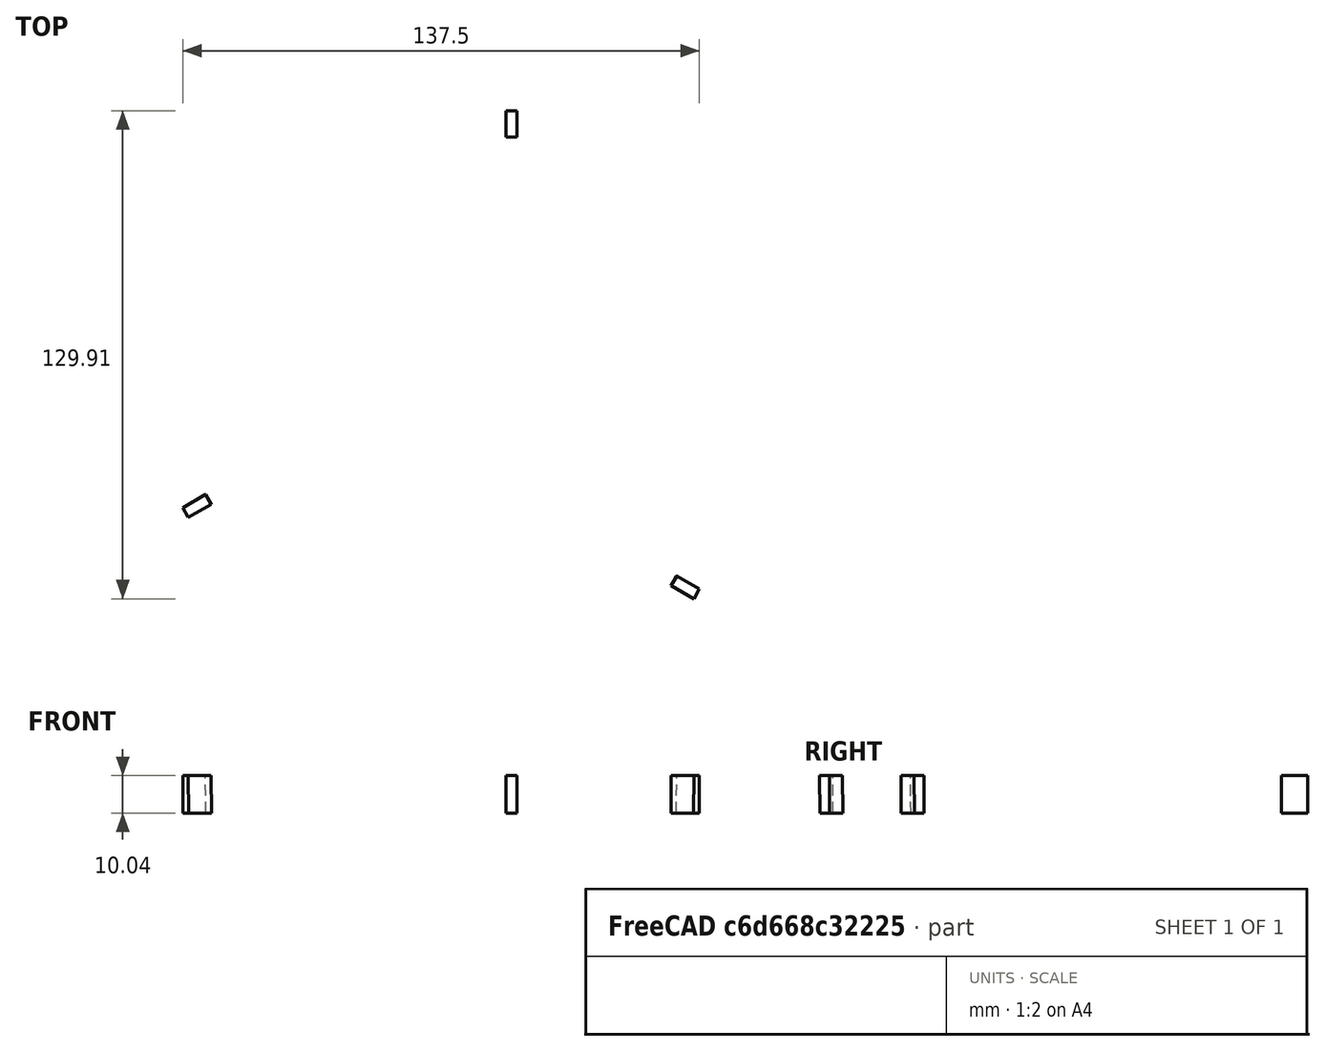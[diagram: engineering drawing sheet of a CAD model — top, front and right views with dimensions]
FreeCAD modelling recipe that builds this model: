
FCSTD DOCUMENT  (FreeCAD 2024.1R35694 (Git))
Label: spreadsheet-example-deltarobot
License: All rights reserved
LicenseURL: http://en.wikipedia.org/wiki/All_rights_reserved
objects: App::FeaturePython×23, App::Link×17, Part::FeaturePython×3, Spreadsheet::Sheet×1, Assembly::JointGroup×1, Assembly::AssemblyObject×1
note: 3 computed .brp shape members not serialized (recipe doc carries the construction recipe); baked Part::Feature solids carry a one-line shape summary decoded from their .brp
EXTERNAL_REF file=base.FCStd obj=Part
EXTERNAL_REF file=nema17-48.FCStd obj=Part
EXTERNAL_REF file=arm.FCStd obj=Part
EXTERNAL_REF file=plate.FCStd obj=Part
EXTERNAL_REF file=link.FCStd obj=Part
EXTERNAL_REF file=cone.FCStd obj=Part

FEATURE [App::Link] base  label="base 🔒"
  LinkedObject = -> <external base.FCStd>#Part
FEATURE [App::Link] nema17_48
  LinkPlacement = pos=(66.4519,-34.9019,1.93e-14) rot=(0.935113,-0.250563,-0.250563;1.63783rad)
  LinkedObject = -> <external nema17-48.FCStd>#Part
  Placement = pos=(66.4519,-34.9019,1.93e-14) rot=(0.935113,-0.250563,-0.250563;1.63783rad)
FEATURE [App::Link] nema17_049
  LinkPlacement = pos=(-63.4519,-40.0981,5.19e-14) rot=(-0.935113,-0.250563,0.250563;1.63783rad)
  LinkedObject = -> <external nema17-48.FCStd>#Part
  Placement = pos=(-63.4519,-40.0981,5.19e-14) rot=(-0.935113,-0.250563,0.250563;1.63783rad)
FEATURE [App::Link] nema17_050
  LinkPlacement = pos=(-3,75,4.6e-15) rot=(0.57735,-0.57735,0.57735;4.18879rad)
  LinkedObject = -> <external nema17-48.FCStd>#Part
  Placement = pos=(-3,75,4.6e-15) rot=(0.57735,-0.57735,0.57735;4.18879rad)
FEATURE [App::FeaturePython] GroundedJoint  # Assembly grounded joint (typed FeaturePython)
  ObjectToGround = -> base
FEATURE [App::FeaturePython] Fixed  # Assembly joint (typed FeaturePython)
  Detach1 = false
  Detach2 = false
  Distance = 0
  Element1 = Edge11
  Element2 = Edge27
  FirstPartConnected = false
  JointType = 0 (Fixed)
  Object1 = Body
  Object2 = Body002
  Offset = (0,0,0)
  Part1 = -> nema17_48
  Part2 = -> base
  Placement1 = pos=(0,0,48) rot=(0,0,1;0rad)
  Placement2 = pos=(67.4519,-33.1699,1.95e-14) rot=(0.935113,-0.250563,-0.250563;1.63783rad)
  Rotation = 0
  Vertex1 = Edge11
  Vertex2 = Edge27
FEATURE [App::FeaturePython] Fixed001  # Assembly joint (typed FeaturePython)
  Detach1 = false
  Detach2 = false
  Distance = 0
  Element1 = Edge11
  Element2 = Edge32
  FirstPartConnected = false
  JointType = 0 (Fixed)
  Object1 = Body
  Object2 = Body002
  Offset = (0,0,0)
  Part1 = -> nema17_049
  Part2 = -> base
  Placement1 = pos=(0,0,48) rot=(0,0,1;0rad)
  Placement2 = pos=(-62.4519,-41.8301,5.28e-14) rot=(-0.186157,0.694747,0.694747;3.50969rad)
  Rotation = 0
  Vertex1 = Edge11
  Vertex2 = Edge32
FEATURE [App::FeaturePython] Fixed002  # Assembly joint (typed FeaturePython)
  Detach1 = false
  Detach2 = false
  Distance = 0
  Element1 = Edge11
  Element2 = Edge12
  FirstPartConnected = false
  JointType = 0 (Fixed)
  Object1 = Body
  Object2 = Body002
  Offset = (0,0,0)
  Part1 = -> nema17_050
  Part2 = -> base
  Placement1 = pos=(0,0,48) rot=(0,0,1;0rad)
  Placement2 = pos=(-5,75,4.4e-15) rot=(0.57735,0.57735,0.57735;2.0944rad)
  Rotation = 0
  Vertex1 = Edge11
  Vertex2 = Edge12
FEATURE [App::Link] arm
  LinkPlacement = pos=(61.4519,-43.5622,1.7e-14) rot=(0.696382,-0.186595,0.69299;2.7744rad)
  LinkedObject = -> <external arm.FCStd>#Part
  Placement = pos=(61.4519,-43.5622,1.7e-14) rot=(0.696382,-0.186595,0.69299;2.7744rad)
FEATURE [App::Link] arm001
  LinkPlacement = pos=(-68.4519,-31.4378,4.95e-14) rot=(0.250639,-0.935398,0.249419;1.6424rad)
  LinkedObject = -> <external arm.FCStd>#Part
  Placement = pos=(-68.4519,-31.4378,4.95e-14) rot=(0.250639,-0.935398,0.249419;1.6424rad)
FEATURE [App::Link] arm002
  LinkPlacement = pos=(7,75,6.4e-15) rot=(0.578288,0.578288,0.575471;4.18597rad)
  LinkedObject = -> <external arm.FCStd>#Part
  Placement = pos=(7,75,6.4e-15) rot=(0.578288,0.578288,0.575471;4.18597rad)
FEATURE [App::FeaturePython] Revolute  # Assembly joint (typed FeaturePython)
  Detach1 = false
  Detach2 = false
  Distance = 0
  Element1 = Edge44
  Element2 = Edge38
  FirstPartConnected = true
  JointType = 1 (Revolute)
  Object1 = Body
  Object2 = Body001
  Offset = (0,0,0)
  Part1 = -> nema17_48
  Part2 = -> arm
  Placement1 = pos=(0,0,50) rot=(1,0,0;3.14159rad)
  Placement2 = pos=(0,-10,6.7e-15) rot=(1,0,0;1.5708rad)
  Rotation = 0
  Vertex1 = Edge44
  Vertex2 = Edge38
FEATURE [App::FeaturePython] Revolute001  # Assembly joint (typed FeaturePython)
  Detach1 = false
  Detach2 = false
  Distance = 0
  Element1 = Edge38
  Element2 = Edge44
  FirstPartConnected = false
  JointType = 1 (Revolute)
  Object1 = Body001
  Object2 = Body
  Offset = (0,0,0)
  Part1 = -> arm001
  Part2 = -> nema17_049
  Placement1 = pos=(0,-10,6.7e-15) rot=(1,0,0;1.5708rad)
  Placement2 = pos=(0,0,50) rot=(1,0,0;3.14159rad)
  Rotation = 0
  Vertex1 = Edge38
  Vertex2 = Edge44
FEATURE [App::FeaturePython] Revolute002  # Assembly joint (typed FeaturePython)
  Detach1 = false
  Detach2 = false
  Distance = 0
  Element1 = Edge38
  Element2 = Edge44
  FirstPartConnected = false
  JointType = 1 (Revolute)
  Object1 = Body001
  Object2 = Body
  Offset = (0,0,0)
  Part1 = -> arm002
  Part2 = -> nema17_050
  Placement1 = pos=(0,-10,6.7e-15) rot=(1,0,0;1.5708rad)
  Placement2 = pos=(0,0,50) rot=(1,0,0;3.14159rad)
  Rotation = 0
  Vertex1 = Edge38
  Vertex2 = Edge44
FEATURE [App::Link] plate  label="plate 🔒"
  LinkPlacement = pos=(0,0,116) rot=(0,0,1;0rad)
  LinkedObject = -> <external plate.FCStd>#Part
  Placement = pos=(0,0,116) rot=(0,0,1;0rad)
FEATURE [App::Link] link
  LinkPlacement = pos=(89.576,-22.8492,57.8706) rot=(-0.676617,0.713401,0.182342;1.52525rad)
  LinkedObject = -> <external link.FCStd>#Part
  Placement = pos=(89.576,-22.8492,57.8706) rot=(-0.676617,0.713401,0.182342;1.52525rad)
FEATURE [App::Link] link001
  LinkPlacement = pos=(64.576,-66.1505,57.8706) rot=(0.826476,0.110324,-0.552056;2.256rad)
  LinkedObject = -> <external link.FCStd>#Part
  Placement = pos=(64.576,-66.1505,57.8706) rot=(0.826476,0.110324,-0.552056;2.256rad)
FEATURE [App::Link] link002
  LinkPlacement = pos=(-64.576,-66.1505,57.8706) rot=(0.161974,0.81154,-0.561398;2.1205rad)
  LinkedObject = -> <external link.FCStd>#Part
  Placement = pos=(-64.576,-66.1505,57.8706) rot=(0.161974,0.81154,-0.561398;2.1205rad)
FEATURE [App::Link] link003
  LinkPlacement = pos=(-89.576,-22.8492,57.8706) rot=(-0.498673,0.455531,0.737439;2.90945rad)
  LinkedObject = -> <external link.FCStd>#Part
  Placement = pos=(-89.576,-22.8492,57.8706) rot=(-0.498673,0.455531,0.737439;2.90945rad)
FEATURE [App::Link] link004
  LinkPlacement = pos=(25,88.9997,57.8706) rot=(0.362835,0.914909,0.176894;1.72299rad)
  LinkedObject = -> <external link.FCStd>#Part
  Placement = pos=(25,88.9997,57.8706) rot=(0.362835,0.914909,0.176894;1.72299rad)
FEATURE [App::Link] link005
  LinkPlacement = pos=(-25,88.9997,57.8706) rot=(0.226144,-0.912799,-0.340083;1.62472rad)
  LinkedObject = -> <external link.FCStd>#Part
  Placement = pos=(-25,88.9997,57.8706) rot=(0.226144,-0.912799,-0.340083;1.62472rad)
FEATURE [App::FeaturePython] Ball  # Assembly joint (typed FeaturePython)
  Detach1 = false
  Detach2 = false
  Distance = 0
  Element1 = Face10
  Element2 = Face17
  FirstPartConnected = false
  JointType = 4 (Ball)
  Object1 = Body
  Object2 = Body001
  Offset = (0,0,0)
  Part1 = -> link
  Part2 = -> arm
  Placement1 = pos=(70,0,0) rot=(1,0,0;3.14159rad)
  Placement2 = pos=(0,-32,53) rot=(0.57735,0.57735,0.57735;4.18879rad)
  Rotation = 0
  Vertex1 = Face10
  Vertex2 = Face17
FEATURE [App::FeaturePython] Ball001  # Assembly joint (typed FeaturePython)
  Detach1 = false
  Detach2 = false
  Distance = 0
  Element1 = Face18
  Element2 = Face9
  FirstPartConnected = false
  JointType = 4 (Ball)
  Object1 = Body001
  Object2 = Body
  Offset = (0,0,0)
  Part1 = -> plate
  Part2 = -> link
  Placement1 = pos=(55.8013,-3.34936,0) rot=(0.935113,-0.250563,-0.250563;1.63783rad)
  Placement2 = pos=(-70,0,0) rot=(0,0,1;3.14159rad)
  Rotation = 0
  Vertex1 = Face18
  Vertex2 = Face9
FEATURE [App::FeaturePython] Ball002  # Assembly joint (typed FeaturePython)
  Detach1 = false
  Detach2 = false
  Distance = 0
  Element1 = Face18
  Element2 = Face10
  FirstPartConnected = true
  JointType = 4 (Ball)
  Object1 = Body001
  Object2 = Body
  Offset = (0,0,0)
  Part1 = -> arm
  Part2 = -> link001
  Placement1 = pos=(0,18,53) rot=(0.57735,0.57735,0.57735;4.18879rad)
  Placement2 = pos=(70,0,0) rot=(1,0,0;3.14159rad)
  Rotation = 0
  Vertex1 = Face18
  Vertex2 = Face10
FEATURE [App::FeaturePython] Ball003  # Assembly joint (typed FeaturePython)
  Detach1 = false
  Detach2 = false
  Distance = 0
  Element1 = Face9
  Element2 = Face17
  FirstPartConnected = true
  JointType = 4 (Ball)
  Object1 = Body
  Object2 = Body001
  Offset = (0,0,0)
  Part1 = -> link001
  Part2 = -> plate
  Placement1 = pos=(-70,0,0) rot=(0,0,1;3.14159rad)
  Placement2 = pos=(30.8013,-46.6506,0) rot=(0.935113,-0.250563,-0.250563;1.63783rad)
  Rotation = 0
  Vertex1 = Face9
  Vertex2 = Face17
FEATURE [App::FeaturePython] Ball004  # Assembly joint (typed FeaturePython)
  Detach1 = false
  Detach2 = false
  Distance = 0
  Element1 = Face17
  Element2 = Face10
  FirstPartConnected = true
  JointType = 4 (Ball)
  Object1 = Body001
  Object2 = Body
  Offset = (0,0,0)
  Part1 = -> arm001
  Part2 = -> link002
  Placement1 = pos=(0,-32,53) rot=(0.57735,0.57735,0.57735;4.18879rad)
  Placement2 = pos=(70,0,0) rot=(1,0,0;3.14159rad)
  Rotation = 0
  Vertex1 = Face17
  Vertex2 = Face10
FEATURE [App::FeaturePython] Ball005  # Assembly joint (typed FeaturePython)
  Detach1 = false
  Detach2 = false
  Distance = 0
  Element1 = Face18
  Element2 = Face10
  FirstPartConnected = true
  JointType = 4 (Ball)
  Object1 = Body001
  Object2 = Body
  Offset = (0,0,0)
  Part1 = -> arm001
  Part2 = -> link003
  Placement1 = pos=(0,18,53) rot=(0.57735,0.57735,0.57735;4.18879rad)
  Placement2 = pos=(70,0,0) rot=(1,0,0;3.14159rad)
  Rotation = 0
  Vertex1 = Face18
  Vertex2 = Face10
FEATURE [App::FeaturePython] Ball006  # Assembly joint (typed FeaturePython)
  Detach1 = false
  Detach2 = false
  Distance = 0
  Element1 = Face3
  Element2 = Face9
  FirstPartConnected = true
  JointType = 4 (Ball)
  Object1 = Body001
  Object2 = Body
  Offset = (0,0,0)
  Part1 = -> plate
  Part2 = -> link002
  Placement1 = pos=(-30.8013,-46.6506,0) rot=(-0.186157,0.694747,0.694747;3.50969rad)
  Placement2 = pos=(-70,0,0) rot=(0,0,1;3.14159rad)
  Rotation = 0
  Vertex1 = Face3
  Vertex2 = Face9
FEATURE [App::FeaturePython] Ball007  # Assembly joint (typed FeaturePython)
  Detach1 = false
  Detach2 = false
  Distance = 0
  Element1 = Face1
  Element2 = Face9
  FirstPartConnected = true
  JointType = 4 (Ball)
  Object1 = Body001
  Object2 = Body
  Offset = (0,0,0)
  Part1 = -> plate
  Part2 = -> link003
  Placement1 = pos=(-55.8013,-3.34936,0) rot=(-0.186157,0.694747,0.694747;3.50969rad)
  Placement2 = pos=(-70,0,0) rot=(0,0,1;3.14159rad)
  Rotation = 0
  Vertex1 = Face1
  Vertex2 = Face9
FEATURE [App::FeaturePython] Ball008  # Assembly joint (typed FeaturePython)
  Detach1 = false
  Detach2 = false
  Distance = 0
  Element1 = Face17
  Element2 = Face9
  FirstPartConnected = true
  JointType = 4 (Ball)
  Object1 = Body001
  Object2 = Body
  Offset = (0,0,0)
  Part1 = -> arm002
  Part2 = -> link005
  Placement1 = pos=(0,-32,53) rot=(0.57735,0.57735,0.57735;4.18879rad)
  Placement2 = pos=(-70,0,0) rot=(0,0,1;3.14159rad)
  Rotation = 0
  Vertex1 = Face17
  Vertex2 = Face9
FEATURE [App::FeaturePython] Ball009  # Assembly joint (typed FeaturePython)
  Detach1 = false
  Detach2 = false
  Distance = 0
  Element1 = Face16
  Element2 = Face10
  FirstPartConnected = true
  JointType = 4 (Ball)
  Object1 = Body001
  Object2 = Body
  Offset = (0,0,0)
  Part1 = -> plate
  Part2 = -> link005
  Placement1 = pos=(-25,50,0) rot=(0.57735,0.57735,0.57735;2.0944rad)
  Placement2 = pos=(70,0,0) rot=(1,0,0;3.14159rad)
  Rotation = 0
  Vertex1 = Face16
  Vertex2 = Face10
FEATURE [App::FeaturePython] Ball010  # Assembly joint (typed FeaturePython)
  Detach1 = false
  Detach2 = false
  Distance = 0
  Element1 = Face18
  Element2 = Face10
  FirstPartConnected = true
  JointType = 4 (Ball)
  Object1 = Body001
  Object2 = Body
  Offset = (0,0,0)
  Part1 = -> arm002
  Part2 = -> link004
  Placement1 = pos=(0,18,53) rot=(0.57735,0.57735,0.57735;4.18879rad)
  Placement2 = pos=(70,0,0) rot=(1,0,0;3.14159rad)
  Rotation = 0
  Vertex1 = Face18
  Vertex2 = Face10
FEATURE [App::FeaturePython] Ball011  # Assembly joint (typed FeaturePython)
  Detach1 = false
  Detach2 = false
  Distance = 0
  Element1 = Face15
  Element2 = Face9
  FirstPartConnected = true
  JointType = 4 (Ball)
  Object1 = Body001
  Object2 = Body
  Offset = (0,0,0)
  Part1 = -> plate
  Part2 = -> link004
  Placement1 = pos=(25,50,0) rot=(0.57735,0.57735,0.57735;2.0944rad)
  Placement2 = pos=(-70,0,0) rot=(0,0,1;3.14159rad)
  Rotation = 0
  Vertex1 = Face15
  Vertex2 = Face9
FEATURE [App::Link] cone
  LinkPlacement = pos=(7,107,-26) rot=(0,0,1;0rad)
  LinkedObject = -> <external cone.FCStd>#Part
  Placement = pos=(7,107,-26) rot=(0,0,1;0rad)
FEATURE [App::Link] cone001
  LinkPlacement = pos=(-96,-48,-26) rot=(0,0,1;0rad)
  LinkedObject = -> <external cone.FCStd>#Part
  Placement = pos=(-96,-48,-26) rot=(0,0,1;0rad)
FEATURE [App::Link] cone002
  LinkPlacement = pos=(92,-61,-26) rot=(0,0,1;0rad)
  LinkedObject = -> <external cone.FCStd>#Part
  Placement = pos=(92,-61,-26) rot=(0,0,1;0rad)
FEATURE [App::FeaturePython] GroundedJoint001  label="PlatePosition"  # Assembly grounded joint (typed FeaturePython)
  ObjectToGround = -> plate
  Placement = pos=(0,0,116) rot=(0,0,1;0rad)
FEATURE [Spreadsheet::Sheet] Spreadsheet
  cells = A1='x; B1='y; C1='z; D1='duration [s]; A2=0; B2=0; C2=116; D2=1.5; A3=-20; B3=0; C3=116; D3=2; A4=10; B4=30; C4=125; D4=2; A5=0; B5=20; C5=150; D5=2; A6=0; B6=0; C6=116; D6=4
FEATURE [Part::FeaturePython] MotorObserver0  # WARN: FeaturePython — macro-defined, semantics opaque (R4)
  Enabled = true
  Placement = pos=(58.7019,-48.3253,1.6e-14) rot=(0.655971,0.376593,0.654125;3.86752rad)
  Reversed = true
  TransfAngle = 360
FEATURE [Part::FeaturePython] MotorObserver1  # WARN: FeaturePython — macro-defined, semantics opaque (R4)
  Enabled = true
  Placement = pos=(-71.2019,-26.6747,4.78e-14) rot=(0.653335,-0.379333,0.655179;2.42206rad)
  Reversed = true
  TransfAngle = 360
FEATURE [Part::FeaturePython] MotorObserver2  # WARN: FeaturePython — macro-defined, semantics opaque (R4)
  Enabled = true
  Placement = pos=(12.5,75,7e-15) rot=(-0.002441,-0.999994,0.002441;1.5708rad)
  Reversed = true
  TransfAngle = 360
FEATURE [App::FeaturePython] Fixed003  # Assembly joint (typed FeaturePython)
  Activated = true
  Detach1 = false
  Detach2 = false
  Distance = 0
  Element1 = Face6
  Element2 = Edge34
  JointType = 0 (Fixed)
  Object1 = MotorObserver0
  Object2 = Body001
  Offset = (0,0,0)
  Part1 = -> MotorObserver0
  Part2 = -> arm
  Placement1 = pos=(2e-16,0,1.5) rot=(0,0,1;0rad)
  Placement2 = pos=(0,4,-2.7e-15) rot=(1,0,0;1.5708rad)
  Rotation = 0
  Vertex1 = Face6
  Vertex2 = Edge34
FEATURE [App::FeaturePython] Fixed004  # Assembly joint (typed FeaturePython)
  Activated = true
  Detach1 = false
  Detach2 = false
  Distance = 0
  Element1 = Face6
  Element2 = Edge34
  JointType = 0 (Fixed)
  Object1 = MotorObserver1
  Object2 = Body001
  Offset = (0,0,0)
  Part1 = -> MotorObserver1
  Part2 = -> arm001
  Placement1 = pos=(2e-16,-1.42e-14,1.5) rot=(0,0,1;0rad)
  Placement2 = pos=(0,4,-2.7e-15) rot=(1,0,0;1.5708rad)
  Rotation = 0
  Vertex1 = Face6
  Vertex2 = Edge34
FEATURE [App::FeaturePython] Fixed005  # Assembly joint (typed FeaturePython)
  Activated = true
  Detach1 = false
  Detach2 = false
  Distance = 0
  Element1 = Face6
  Element2 = Edge34
  JointType = 0 (Fixed)
  Object1 = MotorObserver2
  Object2 = Body001
  Offset = (0,0,0)
  Part1 = -> MotorObserver2
  Part2 = -> arm002
  Placement1 = pos=(2e-16,0,1.5) rot=(0,0,1;0rad)
  Placement2 = pos=(0,4,-2.7e-15) rot=(1,0,0;1.5708rad)
  Rotation = 0
  Vertex1 = Face6
  Vertex2 = Edge34
FEATURE [Assembly::JointGroup] Joints
  Group = -> [GroundedJoint,Fixed,Fixed001,Fixed002,Revolute,Revolute001,Revolute002,Ball,Ball001,Ball002,Ball003,Ball004,Ball005,Ball006,Ball007,Ball008,Ball009,Ball010,Ball011,GroundedJoint001,Fixed003,Fixed004,Fixed005]
FEATURE [Assembly::AssemblyObject] Assembly  label="deltabot"
  Group = -> [Joints,base,nema17_48,nema17_049,nema17_050,GroundedJoint,Fixed,Fixed001,Fixed002,arm,arm001,arm002,Revolute,Revolute001,Revolute002,plate,link,link001,link002,link003,link004,link005,Ball,Ball001,Ball002,Ball003,Ball004,Ball005,Ball006,Ball007,Ball008,Ball009,Ball010,Ball011,cone,cone001,cone002,GroundedJoint001,MotorObserver0,MotorObserver1,MotorObserver2,Fixed003,Fixed004,Fixed005]
  Origin = -> Origin
  Type = Assembly

RESOLVED EXTERNAL PARTS (link-assembly join: the EXTERNAL_REF files above that resolve inside this repo's crawl, each included once):
---- part arm.FCStd = doc fcstd_cb6b5a2d1849 ----
FCSTD DOCUMENT  (FreeCAD 2024.1R35694 (Git))
Label: arm
License: All rights reserved
LicenseURL: http://en.wikipedia.org/wiki/All_rights_reserved
objects: Sketcher::SketchObject×11, PartDesign::Pad×6, PartDesign::Plane×2, PartDesign::Revolution×2, PartDesign::Mirrored×2, PartDesign::Body×2, PartDesign::Pocket×2, PartDesign::Chamfer×1, PartDesign::Hole×1, PartDesign::Fillet×1, App::Part×1
note: 43 computed .brp shape members not serialized (recipe doc carries the construction recipe); baked Part::Feature solids carry a one-line shape summary decoded from their .brp

FEATURE [PartDesign::Plane] DatumPlane002  label="midplane001"
  AttachmentOffset = pos=(0,0,7) rot=(0,0,1;0rad)
  Length = 60
  MapMode = 5
  Placement = pos=(0,-7,1.6e-15) rot=(1,0,0;1.5708rad)
  ResizeMode = 0
  Support = -> [XZ_Plane002]
  Width = 60
FEATURE [Sketcher::SketchObject] Sketch008
  FullyConstrained = true
  MapMode = 5
  Placement = pos=(0,0,0) rot=(1,0,0;1.5708rad)
  Support = -> [XZ_Plane002]
  sketch-geometry (5):
    g0: Circle CenterX=0 CenterY=0 CenterZ=0 NormalX=0 NormalY=0 NormalZ=1 AngleXU=0 Radius=2.5
    g1: ArcOfCircle CenterX=0 CenterY=0 CenterZ=0 NormalX=0 NormalY=0 NormalZ=1 AngleXU=0 Radius=6 StartAngle=3.14159 EndAngle=6.28319
    g2: LineSegment StartX=-6 StartY=-1.9e-15 StartZ=0 EndX=-6 EndY=50 EndZ=0
    g3: LineSegment StartX=6 StartY=-1.5e-15 StartZ=0 EndX=6 EndY=50 EndZ=0
    g4: LineSegment StartX=-6 StartY=50 StartZ=0 EndX=6 EndY=50 EndZ=0
  constraints (12):
    c: Coincident(g0,g-1)
    c: Tangent(g1,g2) = 1.5708
    c: Tangent(g1,g3) = -1.5708
    c: Vertical(g3)
    c: Diameter(g0) = 5
    c: Distance(g1,g1) = 12
    c: PointOnObject(g1,g-1)
    c: Coincident(g4,g2)
    c: Coincident(g4,g3)
    c: DistanceY(g3,g3) = 50
    c: Vertical(g2)
    c: Symmetric(g2,g3,g-2)
FEATURE [PartDesign::Pad] Pad003
  Direction = (0,-1,2e-16)
  Length = 8
  Length2 = 10
  Midplane = true
  Placement = pos=(0,0,0) rot=(1,0,0;1.5708rad)
  Profile = -> Sketch008
  ReferenceAxis = -> Sketch008 [N_Axis]
  Type = 0
FEATURE [Sketcher::SketchObject] Sketch009
  FullyConstrained = true
  MapMode = 5
  Placement = pos=(0,0,0) rot=(1,0,0;1.5708rad)
  Support = -> [XZ_Plane002]
  sketch-geometry (2):
    g0: Circle CenterX=0 CenterY=0 CenterZ=0 NormalX=0 NormalY=0 NormalZ=1 AngleXU=0 Radius=2.5
    g1: Circle CenterX=0 CenterY=0 CenterZ=0 NormalX=0 NormalY=0 NormalZ=1 AngleXU=0 Radius=6
  constraints (4):
    c: Coincident(g0,g-1)
    c: Coincident(g1,g0)
    c: Diameter(g0) = 5
    c: Diameter(g1) = 12
FEATURE [PartDesign::Pad] Pad004
  BaseFeature = -> Pad003
  Direction = (0,-1,2e-16)
  Length = 10
  Length2 = 10
  Placement = pos=(0,0,0) rot=(1,0,0;1.5708rad)
  Profile = -> Sketch009
  ReferenceAxis = -> Sketch009 [N_Axis]
  Refine = true
  Type = 0
FEATURE [Sketcher::SketchObject] Sketch010
  ExternalGeometry = -> [Pad004]
  FullyConstrained = true
  MapMode = 5
  Placement = pos=(0,-7,1.6e-15) rot=(1,0,0;1.5708rad)
  Support = -> [DatumPlane002]
  sketch-geometry (4):
    g0: LineSegment StartX=-6 StartY=50 StartZ=0 EndX=6 EndY=50 EndZ=0
    g1: LineSegment StartX=6 StartY=50 StartZ=0 EndX=6 EndY=56 EndZ=0
    g2: LineSegment StartX=6 StartY=56 StartZ=0 EndX=-6 EndY=56 EndZ=0
    g3: LineSegment StartX=-6 StartY=56 StartZ=0 EndX=-6 EndY=50 EndZ=0
  constraints (10):
    c: Coincident(g0,g1)
    c: Coincident(g1,g2)
    c: Coincident(g2,g3)
    c: Coincident(g3,g0)
    c: Horizontal(g2)
    c: Vertical(g1)
    c: Vertical(g3)
    c: Coincident(g0,g-3)
    c: Coincident(g0,g-3)
    c: DistanceY(g1,g1) = 6
FEATURE [PartDesign::Pad] Pad005
  BaseFeature = -> Pad004
  Direction = (0,-1,2e-16)
  Length = 36
  Length2 = 10
  Midplane = true
  Placement = pos=(0,0,0) rot=(1,0,0;1.5708rad)
  Profile = -> Sketch010
  ReferenceAxis = -> Sketch010 [N_Axis]
  Refine = true
  Type = 0
FEATURE [Sketcher::SketchObject] Sketch011
  ExternalGeometry = -> [Pad005,DatumPlane002]
  FullyConstrained = true
  MapMode = 5
  Placement = pos=(0,0,0) rot=(0.57735,0.57735,0.57735;2.0944rad)
  Support = -> [YZ_Plane002]
  sketch-geometry (4):
    g0: LineSegment StartX=-37 StartY=53 StartZ=0 EndX=-25 EndY=53 EndZ=0
    g1: ArcOfCircle CenterX=-32 CenterY=53 CenterZ=0 NormalX=0 NormalY=0 NormalZ=1 AngleXU=0 Radius=5 StartAngle=0.643501 EndAngle=3.14159
    g2: LineSegment StartX=-28 StartY=56 StartZ=0 EndX=-25 EndY=56 EndZ=0
    g3: LineSegment StartX=-25 StartY=56 StartZ=0 EndX=-25 EndY=53 EndZ=0
  constraints (12):
    c: Symmetric(g-3,g-3,g0)
    c: PointOnObject(g1,g0)
    c: Coincident(g1,g0)
    c: PointOnObject(g0,g-3)
    c: Radius(g1) = 5
    c: Distance(g1,g-4) = 25
    c: Coincident(g1,g2)
    c: PointOnObject(g2,g-3)
    c: Horizontal(g2)
    c: Coincident(g2,g3)
    c: Coincident(g3,g0)
    c: DistanceY(g0,g2) = 3
FEATURE [PartDesign::Revolution] Revolution
  Angle = 360
  Angle2 = 60
  Axis = (0,1,0)
  Base = (0,-37,53)
  BaseFeature = -> Pad005
  Placement = pos=(0,0,0) rot=(1,0,0;1.5708rad)
  Profile = -> Sketch011
  ReferenceAxis = -> Sketch011 [Edge1]
  Refine = true
  Type = 0
FEATURE [PartDesign::Mirrored] Mirrored002
  BaseFeature = -> Revolution
  MirrorPlane = -> DatumPlane002
  Originals = -> [Revolution]
  Placement = pos=(0,0,0) rot=(1,0,0;1.5708rad)
  Refine = true
FEATURE [PartDesign::Body] Body001  label="arm-skeleton"
  Group = -> [Sketch008,Pad003,Sketch009,Pad004,DatumPlane002,Sketch010,Pad005,Sketch011,Revolution,Mirrored002]
  Origin = -> Origin002
  Tip = -> Mirrored002
FEATURE [PartDesign::Plane] DatumPlane003  label="midplane002"
  AttachmentOffset = pos=(0,0,7) rot=(0,0,1;0rad)
  Length = 60
  MapMode = 5
  Placement = pos=(0,-7,1.6e-15) rot=(1,0,0;1.5708rad)
  ResizeMode = 0
  Support = -> [XZ_Plane002]
  Width = 60
FEATURE [Sketcher::SketchObject] Sketch012
  FullyConstrained = true
  MapMode = 5
  Placement = pos=(0,0,0) rot=(1,0,0;1.5708rad)
  Support = -> [XZ_Plane003]
  sketch-geometry (5):
    g0: Circle CenterX=0 CenterY=0 CenterZ=0 NormalX=0 NormalY=0 NormalZ=1 AngleXU=0 Radius=2.5
    g1: ArcOfCircle CenterX=0 CenterY=0 CenterZ=0 NormalX=0 NormalY=0 NormalZ=1 AngleXU=0 Radius=6 StartAngle=3.14159 EndAngle=6.28319
    g2: LineSegment StartX=-6 StartY=-1.9e-15 StartZ=0 EndX=-6 EndY=50 EndZ=0
    g3: LineSegment StartX=6 StartY=-1.5e-15 StartZ=0 EndX=6 EndY=50 EndZ=0
    g4: LineSegment StartX=-6 StartY=50 StartZ=0 EndX=6 EndY=50 EndZ=0
  constraints (12):
    c: Coincident(g0,g-1)
    c: Tangent(g1,g2) = 1.5708
    c: Tangent(g1,g3) = -1.5708
    c: Vertical(g3)
    c: Diameter(g0) = 5
    c: Distance(g1,g1) = 12
    c: PointOnObject(g1,g-1)
    c: Coincident(g4,g2)
    c: Coincident(g4,g3)
    c: DistanceY(g3,g3) = 50
    c: Vertical(g2)
    c: Symmetric(g2,g3,g-2)
FEATURE [PartDesign::Pad] Pad006
  Direction = (0,-1,2e-16)
  Length = 8
  Length2 = 10
  Midplane = true
  Placement = pos=(0,0,0) rot=(1,0,0;1.5708rad)
  Profile = -> Sketch012
  ReferenceAxis = -> Sketch012 [N_Axis]
  Type = 0
FEATURE [Sketcher::SketchObject] Sketch013
  FullyConstrained = true
  MapMode = 5
  Placement = pos=(0,0,0) rot=(1,0,0;1.5708rad)
  Support = -> [XZ_Plane003]
  sketch-geometry (2):
    g0: Circle CenterX=0 CenterY=0 CenterZ=0 NormalX=0 NormalY=0 NormalZ=1 AngleXU=0 Radius=2.5
    g1: Circle CenterX=0 CenterY=0 CenterZ=0 NormalX=0 NormalY=0 NormalZ=1 AngleXU=0 Radius=6
  constraints (4):
    c: Coincident(g0,g-1)
    c: Coincident(g1,g0)
    c: Diameter(g0) = 5
    c: Diameter(g1) = 12
FEATURE [PartDesign::Pad] Pad007
  BaseFeature = -> Pad006
  Direction = (0,-1,2e-16)
  Length = 10
  Length2 = 10
  Placement = pos=(0,0,0) rot=(1,0,0;1.5708rad)
  Profile = -> Sketch013
  ReferenceAxis = -> Sketch013 [N_Axis]
  Refine = true
  Type = 0
FEATURE [Sketcher::SketchObject] Sketch014
  ExternalGeometry = -> [Pad007]
  FullyConstrained = true
  MapMode = 5
  Placement = pos=(0,-7,1.6e-15) rot=(1,0,0;1.5708rad)
  Support = -> [DatumPlane003]
  sketch-geometry (4):
    g0: LineSegment StartX=-6 StartY=50 StartZ=0 EndX=6 EndY=50 EndZ=0
    g1: LineSegment StartX=6 StartY=50 StartZ=0 EndX=6 EndY=56 EndZ=0
    g2: LineSegment StartX=6 StartY=56 StartZ=0 EndX=-6 EndY=56 EndZ=0
    g3: LineSegment StartX=-6 StartY=56 StartZ=0 EndX=-6 EndY=50 EndZ=0
  constraints (10):
    c: Coincident(g0,g1)
    c: Coincident(g1,g2)
    c: Coincident(g2,g3)
    c: Coincident(g3,g0)
    c: Horizontal(g2)
    c: Vertical(g1)
    c: Vertical(g3)
    c: Coincident(g0,g-3)
    c: Coincident(g0,g-3)
    c: DistanceY(g1,g1) = 6
FEATURE [PartDesign::Pad] Pad008
  BaseFeature = -> Pad007
  Direction = (0,-1,2e-16)
  Length = 36
  Length2 = 10
  Midplane = true
  Placement = pos=(0,0,0) rot=(1,0,0;1.5708rad)
  Profile = -> Sketch014
  ReferenceAxis = -> Sketch014 [N_Axis]
  Refine = true
  Type = 0
FEATURE [Sketcher::SketchObject] Sketch015
  ExternalGeometry = -> [Pad008,DatumPlane003]
  FullyConstrained = true
  MapMode = 5
  Placement = pos=(0,0,0) rot=(0.57735,0.57735,0.57735;2.0944rad)
  Support = -> [YZ_Plane003]
  sketch-geometry (4):
    g0: LineSegment StartX=-36.9 StartY=53 StartZ=0 EndX=-25 EndY=53 EndZ=0
    g1: ArcOfCircle CenterX=-32 CenterY=53 CenterZ=0 NormalX=0 NormalY=0 NormalZ=1 AngleXU=0 Radius=4.9 StartAngle=0.658897 EndAngle=3.14159
    g2: LineSegment StartX=-28.1257 StartY=56 StartZ=0 EndX=-25 EndY=56 EndZ=0
    g3: LineSegment StartX=-25 StartY=56 StartZ=0 EndX=-25 EndY=53 EndZ=0
  constraints (12):
    c: Symmetric(g-3,g-3,g0)
    c: PointOnObject(g1,g0)
    c: Coincident(g1,g0)
    c: PointOnObject(g0,g-3)
    c: Radius(g1) = 4.9
    c: Distance(g1,g-4) = 25
    c: Coincident(g1,g2)
    c: PointOnObject(g2,g-3)
    c: Horizontal(g2)
    c: Coincident(g2,g3)
    c: Coincident(g3,g0)
    c: DistanceY(g0,g2) = 3
FEATURE [PartDesign::Revolution] Revolution001
  Angle = 360
  Angle2 = 60
  Axis = (0,1,0)
  Base = (0,-36.9,53)
  BaseFeature = -> Pad008
  Placement = pos=(0,0,0) rot=(1,0,0;1.5708rad)
  Profile = -> Sketch015
  ReferenceAxis = -> Sketch015 [Edge1]
  Refine = true
  Type = 0
FEATURE [PartDesign::Mirrored] Mirrored003
  BaseFeature = -> Revolution001
  MirrorPlane = -> DatumPlane003
  Originals = -> [Revolution001]
  Placement = pos=(0,0,0) rot=(1,0,0;1.5708rad)
  Refine = true
FEATURE [PartDesign::Chamfer] Chamfer
  Angle = 45
  Base = -> Mirrored003 [Edge12,Edge10,Edge17,Edge21]
  BaseFeature = -> Mirrored003
  ChamferType = 0
  FlipDirection = false
  Placement = pos=(0,0,0) rot=(1,0,0;1.5708rad)
  Refine = true
  Size = 2
  Size2 = 1
  SupportTransform = false
  UseAllEdges = false
FEATURE [Sketcher::SketchObject] Sketch
  FullyConstrained = true
  MapMode = 5
  Placement = pos=(0,0,0) rot=(1,0,0;1.5708rad)
  Support = -> [XZ_Plane003]
  sketch-geometry (4):
    g0: LineSegment StartX=0.5 StartY=0 StartZ=0 EndX=0.5 EndY=10 EndZ=0
    g1: LineSegment StartX=0.5 StartY=10 StartZ=0 EndX=-0.5 EndY=10 EndZ=0
    g2: LineSegment StartX=-0.5 StartY=10 StartZ=0 EndX=-0.5 EndY=0 EndZ=0
    g3: LineSegment StartX=-0.5 StartY=0 StartZ=0 EndX=0.5 EndY=0 EndZ=0
  constraints (11):
    c: Coincident(g0,g1)
    c: Coincident(g1,g2)
    c: Coincident(g2,g3)
    c: Coincident(g3,g0)
    c: Vertical(g0)
    c: Vertical(g2)
    c: Horizontal(g1)
    c: Horizontal(g3)
    c: Symmetric(g2,g0,g-1)
    c: Distance(g1,g1) = 1
    c: DistanceY(g0,g0) = 10
FEATURE [PartDesign::Pocket] Pocket
  BaseFeature = -> Chamfer
  Direction = (0,1,-2e-16)
  Length = 5
  Length2 = 5
  Midplane = true
  Placement = pos=(0,0,0) rot=(1,0,0;1.5708rad)
  Profile = -> Sketch
  ReferenceAxis = -> Sketch [N_Axis]
  Refine = true
  Type = 1
FEATURE [Sketcher::SketchObject] Sketch016
  FullyConstrained = true
  MapMode = 5
  Placement = pos=(6,0,0) rot=(0.707107,0,0.707107;3.14159rad)
  Support = -> [Pocket]
  sketch-geometry (1):
    g0: Circle CenterX=5 CenterY=0 CenterZ=0 NormalX=0 NormalY=0 NormalZ=1 AngleXU=0 Radius=1.5
  constraints (3):
    c: PointOnObject(g0,g-1)
    c: Diameter(g0) = 3
    c: DistanceX(g-1,g0) = 5
FEATURE [PartDesign::Hole] Hole
  BaseFeature = -> Pocket
  CustomThreadClearance = 0
  Depth = 178.805
  DepthType = 1
  Diameter = 3.4
  DrillForDepth = false
  DrillPoint = 1
  DrillPointAngle = 118
  HoleCutCountersinkAngle = 90
  HoleCutCustomValues = false
  HoleCutDepth = 0
  HoleCutDiameter = 6.1
  HoleCutType = 0
  ModelThread = false
  Placement = pos=(0,0,0) rot=(1,0,0;1.5708rad)
  Profile = -> Sketch016
  Refine = true
  Tapered = false
  TaperedAngle = 90
  ThreadClass = 0
  ThreadDepth = 178.805
  ThreadDepthType = 0
  ThreadDirection = 0
  ThreadFit = 0
  ThreadSize = 9
  ThreadType = 1
  Threaded = false
  UseCustomThreadClearance = false
FEATURE [Sketcher::SketchObject] Sketch017
  ExternalGeometry = -> [Hole]
  FullyConstrained = true
  MapMode = 5
  Placement = pos=(-6,0,0) rot=(0.707107,0,-0.707107;3.14159rad)
  Support = -> [Hole]
  sketch-geometry (7):
    g0: LineSegment StartX=-1.5359 StartY=-4e-16 StartZ=0 EndX=-3.26795 EndY=3 EndZ=0
    g1: LineSegment StartX=-3.26795 StartY=3 StartZ=0 EndX=-6.73205 EndY=3 EndZ=0
    g2: LineSegment StartX=-6.73205 StartY=3 StartZ=0 EndX=-8.4641 EndY=-9e-16 EndZ=0
    g3: LineSegment StartX=-8.4641 StartY=-9e-16 StartZ=0 EndX=-6.73205 EndY=-3 EndZ=0
    g4: LineSegment StartX=-6.73205 StartY=-3 StartZ=0 EndX=-3.26795 EndY=-3 EndZ=0
    g5: LineSegment StartX=-3.26795 StartY=-3 StartZ=0 EndX=-1.5359 EndY=-4e-16 EndZ=0
    g6: Circle CenterX=-5 CenterY=-6e-16 CenterZ=0 NormalX=0 NormalY=0 NormalZ=1 AngleXU=0 Radius=3.4641
  constraints (16):
    c: Coincident(g0,g1)
    c: Coincident(g1,g2)
    c: Coincident(g2,g3)
    c: Coincident(g3,g4)
    c: Coincident(g4,g5)
    c: Coincident(g5,g0)
    c: Equal(g0, g1-g5) x5
    c: PointOnObject(g0,g6)
    c: PointOnObject(g1,g6)
    c: PointOnObject(g2,g6)
    c: PointOnObject(g3,g6)
    c: PointOnObject(g4,g6)
    c: PointOnObject(g5,g6)
    c: Coincident(g6,g-3)
    c: DistanceY(g4,g0) = 6
    c: Horizontal(g1)
FEATURE [PartDesign::Pocket] Pocket001
  BaseFeature = -> Hole
  Direction = (1,0,2e-16)
  Length = 3
  Length2 = 5
  Placement = pos=(0,0,0) rot=(1,0,0;1.5708rad)
  Profile = -> Sketch017
  ReferenceAxis = -> Sketch017 [N_Axis]
  Refine = true
  Type = 0
FEATURE [PartDesign::Fillet] Fillet
  Base = -> Pocket001 [Edge3,Edge46]
  BaseFeature = -> Pocket001
  Placement = pos=(0,0,0) rot=(1,0,0;1.5708rad)
  Radius = 2
  Refine = true
  SupportTransform = false
  UseAllEdges = false
FEATURE [PartDesign::Body] Body002  label="arm0"
  Group = -> [Sketch012,Pad006,Sketch013,Pad007,DatumPlane003,Sketch014,Pad008,Sketch015,Revolution001,Mirrored003,Chamfer,Sketch,Pocket,Sketch016,Hole,Sketch017,Pocket001,Fillet]
  Origin = -> Origin003
  Tip = -> Fillet
FEATURE [App::Part] Part  label="arm"
  Group = -> [Body001,Body002]
  Origin = -> Origin
---- part base.FCStd = doc fcstd_4bb8bb395458 ----
FCSTD DOCUMENT  (FreeCAD 0.22R35451 (Git))
Label: base
License: All rights reserved
LicenseURL: http://en.wikipedia.org/wiki/All_rights_reserved
objects: Sketcher::SketchObject×7, PartDesign::Pad×5, PartDesign::Plane×4, PartDesign::PolarPattern×3, PartDesign::Body×2, PartDesign::Hole×1, PartDesign::Pocket×1, App::Part×1
note: 30 computed .brp shape members not serialized (recipe doc carries the construction recipe); baked Part::Feature solids carry a one-line shape summary decoded from their .brp

FEATURE [PartDesign::Plane] DatumPlane
  Length = 60
  MapMode = 5
  Placement = pos=(0,0,0) rot=(0.57735,0.57735,0.57735;2.0944rad)
  ResizeMode = 0
  Support = -> [YZ_Plane002]
  Width = 60
FEATURE [Sketcher::SketchObject] Sketch001
  FullyConstrained = true
  MapMode = 5
  Placement = pos=(0,0,0) rot=(0.57735,0.57735,0.57735;2.0944rad)
  Support = -> [DatumPlane]
  sketch-geometry (5):
    g0: Circle CenterX=75 CenterY=0 CenterZ=0 NormalX=0 NormalY=0 NormalZ=1 AngleXU=0 Radius=11.25
    g1: LineSegment StartX=96 StartY=21 StartZ=0 EndX=0 EndY=21 EndZ=0
    g2: LineSegment StartX=0 StartY=21 StartZ=0 EndX=0 EndY=-26 EndZ=0
    g3: LineSegment StartX=0 StartY=-26 StartZ=0 EndX=96 EndY=-26 EndZ=0
    g4: LineSegment StartX=96 StartY=-26 StartZ=0 EndX=96 EndY=21 EndZ=0
  constraints (15):
    c: PointOnObject(g0,g-1)
    c: Diameter(g0) = 22.5
    c: DistanceX(g-1,g0) = 75
    c: Coincident(g1,g2)
    c: Coincident(g2,g3)
    c: Coincident(g3,g4)
    c: Coincident(g4,g1)
    c: Horizontal(g1)
    c: Horizontal(g3)
    c: Vertical(g2)
    c: PointOnObject(g2,g-2)
    c: DistanceX(g0,g1) = 21
    c: DistanceY(g-1,g1) = 21
    c: DistanceY(g3,g-1) = 26
    c: Vertical(g4)
FEATURE [PartDesign::Pad] Pad001
  Direction = (1,0,0)
  Length = 5
  Length2 = 10
  Placement = pos=(0,0,0) rot=(0.57735,0.57735,0.57735;2.0944rad)
  Profile = -> Sketch001
  ReferenceAxis = -> Sketch001 [N_Axis]
  Reversed = true
  Type = 0
FEATURE [Sketcher::SketchObject] Sketch002
  ExternalGeometry = -> [Pad001]
  FullyConstrained = true
  MapMode = 5
  Placement = pos=(0,0,0) rot=(0.57735,0.57735,0.57735;2.0944rad)
  Support = -> [Pad001]
  sketch-geometry (5):
    g0: Circle CenterX=90.5 CenterY=15.5 CenterZ=0 NormalX=0 NormalY=0 NormalZ=1 AngleXU=0 Radius=2
    g1: LineSegment StartX=75 StartY=0 StartZ=0 EndX=75 EndY=11.25 EndZ=0
    g2: Circle CenterX=90.5 CenterY=-15.5 CenterZ=0 NormalX=0 NormalY=0 NormalZ=1 AngleXU=0 Radius=2
    g3: Circle CenterX=59.5 CenterY=-15.5 CenterZ=0 NormalX=0 NormalY=0 NormalZ=1 AngleXU=0 Radius=2
    g4: Circle CenterX=59.5 CenterY=15.5 CenterZ=0 NormalX=0 NormalY=0 NormalZ=1 AngleXU=0 Radius=2
  constraints (12):
    c: Coincident(g1,g-3)
    c: PointOnObject(g1,g-3)
    c: Vertical(g1)
    c: Symmetric(g0,g4,g1)
    c: Symmetric(g0,g2,g-1)
    c: Symmetric(g2,g3,g1)
    c: Equal(g4,g0)
    c: Equal(g0,g2)
    c: Equal(g2,g3)
    c: DistanceX(g4,g0) = 31
    c: DistanceY(g2,g0) = 31
    c: Diameter(g0) = 4
FEATURE [PartDesign::Hole] Hole
  BaseFeature = -> Pad001
  CustomThreadClearance = 0
  Depth = 25
  DepthType = 0
  Diameter = 3.4
  DrillForDepth = false
  DrillPoint = 1
  DrillPointAngle = 118
  HoleCutCountersinkAngle = 90
  HoleCutCustomValues = false
  HoleCutDepth = 3.4
  HoleCutDiameter = 6.1
  HoleCutType = 1
  ModelThread = false
  Placement = pos=(0,0,0) rot=(0.57735,0.57735,0.57735;2.0944rad)
  Profile = -> Sketch002
  Tapered = false
  TaperedAngle = 90
  ThreadClass = 0
  ThreadDepth = 25
  ThreadDepthType = 0
  ThreadDirection = 0
  ThreadFit = 0
  ThreadSize = 9
  ThreadType = 1
  Threaded = false
  UseCustomThreadClearance = false
FEATURE [PartDesign::Plane] DatumPlane001
  Length = 60
  MapMode = 5
  Placement = pos=(2.9e-15,0,-26) rot=(0.707107,0.707107,0;3.14159rad)
  ResizeMode = 0
  Support = -> [Pad001]
  Width = 60
FEATURE [Sketcher::SketchObject] Sketch003
  FullyConstrained = true
  MapMode = 5
  Placement = pos=(2.9e-15,0,-26) rot=(0.707107,0.707107,0;3.14159rad)
  Support = -> [DatumPlane001]
  sketch-geometry (1):
    g0: Circle CenterX=0 CenterY=0 CenterZ=0 NormalX=0 NormalY=0 NormalZ=1 AngleXU=0 Radius=5
  constraints (2):
    c: Coincident(g0,g-1)
    c: Diameter(g0) = 10
FEATURE [PartDesign::Pad] Pad002
  BaseFeature = -> Hole
  Direction = (0,0,-1)
  Length = 42
  Length2 = 10
  Placement = pos=(0,0,0) rot=(0.57735,0.57735,0.57735;2.0944rad)
  Profile = -> Sketch003
  ReferenceAxis = -> Sketch003 [N_Axis]
  Refine = true
  Reversed = true
  Type = 1
FEATURE [PartDesign::PolarPattern] PolarPattern
  Angle = 360
  Axis = -> Z_Axis002
  BaseFeature = -> Pad002
  Mode = 0
  Occurrences = 3
  Offset = 120
  Originals = -> [Pad001,Hole]
  Placement = pos=(0,0,0) rot=(0.57735,0.57735,0.57735;2.0944rad)
  Refine = true
FEATURE [Sketcher::SketchObject] Sketch
  FullyConstrained = true
  MapMode = 5
  Placement = pos=(2.9e-15,0,-26) rot=(0.707107,0.707107,0;3.14159rad)
  Support = -> [DatumPlane001]
  sketch-geometry (8):
    g0: LineSegment StartX=96 StartY=0 StartZ=0 EndX=-48 EndY=83.1384 EndZ=0
    g1: LineSegment StartX=-48 StartY=83.1384 StartZ=0 EndX=-48 EndY=-83.1384 EndZ=0
    g2: LineSegment StartX=-48 StartY=-83.1384 StartZ=0 EndX=96 EndY=0 EndZ=0
    g3: Circle CenterX=0 CenterY=0 CenterZ=0 NormalX=0 NormalY=0 NormalZ=1 AngleXU=0 Radius=96
    g4: LineSegment StartX=60 StartY=0 StartZ=0 EndX=-30 EndY=51.9615 EndZ=0
    g5: LineSegment StartX=-30 StartY=51.9615 StartZ=0 EndX=-30 EndY=-51.9615 EndZ=0
    g6: LineSegment StartX=-30 StartY=-51.9615 StartZ=0 EndX=60 EndY=0 EndZ=0
    g7: Circle CenterX=0 CenterY=0 CenterZ=0 NormalX=0 NormalY=0 NormalZ=1 AngleXU=0 Radius=60
  constraints (22):
    c: Coincident(g0,g1)
    c: Coincident(g1,g2)
    c: Coincident(g2,g0)
    c: Equal(g0,g1)
    c: Equal(g0,g2)
    c: PointOnObject(g0,g3)
    c: PointOnObject(g1,g3)
    c: PointOnObject(g2,g3)
    c: Coincident(g3,g-1)
    c: PointOnObject(g2,g-1)
    c: Coincident(g4,g5)
    c: Coincident(g5,g6)
    c: Coincident(g6,g4)
    c: Equal(g4,g5)
    c: Equal(g4,g6)
    c: PointOnObject(g4,g7)
    c: PointOnObject(g5,g7)
    c: PointOnObject(g6,g7)
    c: Coincident(g7,g3)
    c: PointOnObject(g6,g-1)
    c: DistanceX(g-1,g0) = 96
    c: DistanceX(g-1,g4) = 60
FEATURE [PartDesign::Pad] Pad
  BaseFeature = -> PolarPattern
  Direction = (0,0,-1)
  Length = 4
  Length2 = 10
  Placement = pos=(0,0,0) rot=(0.57735,0.57735,0.57735;2.0944rad)
  Profile = -> Sketch
  ReferenceAxis = -> Sketch [N_Axis]
  Refine = true
  Reversed = true
  Type = 0
FEATURE [Sketcher::SketchObject] Sketch004
  ExternalGeometry = -> [Pad]
  FullyConstrained = true
  MapMode = 5
  Placement = pos=(0,0,0) rot=(0.57735,0.57735,0.57735;2.0944rad)
  Support = -> [YZ_Plane002]
  sketch-geometry (4):
    g0: LineSegment StartX=82 StartY=21 StartZ=0 EndX=68 EndY=21 EndZ=0
    g1: LineSegment StartX=68 StartY=21 StartZ=0 EndX=68 EndY=8.80696 EndZ=0
    g2: LineSegment StartX=68 StartY=8.80696 StartZ=0 EndX=82 EndY=8.80696 EndZ=0
    g3: LineSegment StartX=82 StartY=8.80696 StartZ=0 EndX=82 EndY=21 EndZ=0
  constraints (12):
    c: Coincident(g0,g1)
    c: Coincident(g1,g2)
    c: Coincident(g2,g3)
    c: Coincident(g3,g0)
    c: Horizontal(g0)
    c: Horizontal(g2)
    c: Vertical(g1)
    c: Vertical(g3)
    c: PointOnObject(g0,g-4)
    c: PointOnObject(g1,g-3)
    c: PointOnObject(g2,g-3)
    c: DistanceX(g0,g0) = 14
FEATURE [PartDesign::Pocket] Pocket
  BaseFeature = -> Pad
  Direction = (-1,0,0)
  Length = 5
  Length2 = 5
  Placement = pos=(0,0,0) rot=(0.57735,0.57735,0.57735;2.0944rad)
  Profile = -> Sketch004
  ReferenceAxis = -> Sketch004 [N_Axis]
  Refine = true
  Type = 0
FEATURE [PartDesign::PolarPattern] PolarPattern001
  Angle = 360
  Axis = -> Z_Axis002
  BaseFeature = -> Pocket
  Mode = 0
  Occurrences = 3
  Offset = 120
  Originals = -> [Pocket]
  Placement = pos=(0,0,0) rot=(0.57735,0.57735,0.57735;2.0944rad)
  Refine = true
FEATURE [PartDesign::Body] Body001  label="base0"
  Group = -> [DatumPlane,Sketch001,Pad001,DatumPlane001,Sketch002,Hole,Sketch003,Pad002,PolarPattern,Sketch,Pad,Sketch004,Pocket,PolarPattern001]
  Origin = -> Origin002
  Tip = -> PolarPattern001
FEATURE [PartDesign::Plane] DatumPlane002
  Length = 60
  MapMode = 5
  Placement = pos=(0,0,0) rot=(0.57735,0.57735,0.57735;2.0944rad)
  ResizeMode = 0
  Support = -> [YZ_Plane003]
  Width = 60
FEATURE [Sketcher::SketchObject] Sketch006
  FullyConstrained = true
  MapMode = 5
  Placement = pos=(0,0,0) rot=(0.57735,0.57735,0.57735;2.0944rad)
  Support = -> [DatumPlane002]
  sketch-geometry (5):
    g0: Circle CenterX=75 CenterY=0 CenterZ=0 NormalX=0 NormalY=0 NormalZ=1 AngleXU=0 Radius=11.25
    g1: LineSegment StartX=96 StartY=21 StartZ=0 EndX=0 EndY=21 EndZ=0
    g2: LineSegment StartX=0 StartY=21 StartZ=0 EndX=0 EndY=-26 EndZ=0
    g3: LineSegment StartX=0 StartY=-26 StartZ=0 EndX=96 EndY=-26 EndZ=0
    g4: LineSegment StartX=96 StartY=-26 StartZ=0 EndX=96 EndY=21 EndZ=0
  constraints (15):
    c: PointOnObject(g0,g-1)
    c: Diameter(g0) = 22.5
    c: DistanceX(g-1,g0) = 75
    c: Coincident(g1,g2)
    c: Coincident(g2,g3)
    c: Coincident(g3,g4)
    c: Coincident(g4,g1)
    c: Horizontal(g1)
    c: Horizontal(g3)
    c: Vertical(g2)
    c: PointOnObject(g2,g-2)
    c: DistanceX(g0,g1) = 21
    c: DistanceY(g-1,g1) = 21
    c: DistanceY(g3,g-1) = 26
    c: Vertical(g4)
FEATURE [PartDesign::Pad] Pad004
  Direction = (1,0,0)
  Length = 5
  Length2 = 10
  Placement = pos=(0,0,0) rot=(0.57735,0.57735,0.57735;2.0944rad)
  Profile = -> Sketch006
  ReferenceAxis = -> Sketch006 [N_Axis]
  Reversed = true
  Type = 0
FEATURE [PartDesign::Plane] DatumPlane003
  Length = 60
  MapMode = 5
  Placement = pos=(2.9e-15,0,-26) rot=(0.707107,0.707107,0;3.14159rad)
  ResizeMode = 0
  Support = -> [Pad004]
  Width = 60
FEATURE [Sketcher::SketchObject] Sketch008
  FullyConstrained = true
  MapMode = 5
  Placement = pos=(2.9e-15,0,-26) rot=(0.707107,0.707107,0;3.14159rad)
  Support = -> [DatumPlane003]
  sketch-geometry (1):
    g0: Circle CenterX=0 CenterY=0 CenterZ=0 NormalX=0 NormalY=0 NormalZ=1 AngleXU=0 Radius=5
  constraints (2):
    c: Coincident(g0,g-1)
    c: Diameter(g0) = 10
FEATURE [PartDesign::Pad] Pad005
  BaseFeature = -> Pad004
  Direction = (0,0,-1)
  Length = 42
  Length2 = 10
  Placement = pos=(0,0,0) rot=(0.57735,0.57735,0.57735;2.0944rad)
  Profile = -> Sketch008
  ReferenceAxis = -> Sketch008 [N_Axis]
  Refine = true
  Reversed = true
  Type = 1
FEATURE [PartDesign::PolarPattern] PolarPattern002
  Angle = 360
  Axis = -> Z_Axis003
  BaseFeature = -> Pad005
  Mode = 0
  Occurrences = 3
  Offset = 120
  Originals = -> [Pad004]
  Placement = pos=(0,0,0) rot=(0.57735,0.57735,0.57735;2.0944rad)
  Refine = true
FEATURE [PartDesign::Body] Body002  label="base-skeleton"
  Group = -> [DatumPlane002,Sketch006,Pad004,DatumPlane003,Sketch008,Pad005,PolarPattern002]
  Origin = -> Origin003
  Tip = -> PolarPattern002
FEATURE [App::Part] Part  label="base"
  Group = -> [Body002,Body001]
  Origin = -> Origin
---- part cone.FCStd = doc fcstd_c84bd6ce8fa1 ----
FCSTD DOCUMENT  (FreeCAD 0.22R35451 (Git))
Label: cone
License: All rights reserved
LicenseURL: http://en.wikipedia.org/wiki/All_rights_reserved
objects: Sketcher::SketchObject×1, PartDesign::Revolution×1, PartDesign::Body×1, App::Part×1
note: 4 computed .brp shape members not serialized (recipe doc carries the construction recipe); baked Part::Feature solids carry a one-line shape summary decoded from their .brp

FEATURE [Sketcher::SketchObject] Sketch
  FullyConstrained = true
  MapMode = 5
  Placement = pos=(0,0,0) rot=(1,0,0;1.5708rad)
  Support = -> [XZ_Plane001]
  sketch-geometry (4):
    g0: LineSegment StartX=0 StartY=0 StartZ=0 EndX=0 EndY=20 EndZ=0
    g1: LineSegment StartX=0 StartY=20 StartZ=0 EndX=2 EndY=20 EndZ=0
    g2: ArcOfCircle CenterX=31 CenterY=20 CenterZ=0 NormalX=0 NormalY=0 NormalZ=1 AngleXU=0 Radius=29 StartAngle=3.14159 EndAngle=3.90261
    g3: LineSegment StartX=10 StartY=0 StartZ=0 EndX=0 EndY=0 EndZ=0
  constraints (11):
    c: Coincident(g-1,g0)
    c: PointOnObject(g0,g-2)
    c: Coincident(g0,g1)
    c: Horizontal(g1)
    c: Perpendicular(g1,g2) = 4.71239
    c: PointOnObject(g2,g-1)
    c: Coincident(g2,g3)
    c: Coincident(g3,g0)
    c: DistanceX(g1,g1) = 2
    c: DistanceX(g3,g3) = 10
    c: DistanceY(g0,g0) = 20
FEATURE [PartDesign::Revolution] Revolution
  Angle = 360
  Angle2 = 60
  Axis = (0,2e-16,1)
  Base = (0,0,0)
  Placement = pos=(0,0,0) rot=(1,0,0;1.5708rad)
  Profile = -> Sketch
  ReferenceAxis = -> Sketch [V_Axis]
  Refine = true
  Reversed = true
  Type = 0
FEATURE [PartDesign::Body] Body  label="cone0"
  Group = -> [Sketch,Revolution]
  Origin = -> Origin001
  Tip = -> Revolution
FEATURE [App::Part] Part  label="cone"
  Group = -> [Body]
  Origin = -> Origin
---- part link.FCStd = doc fcstd_2a591de467ad ----
FCSTD DOCUMENT  (FreeCAD 0.22R35451 (Git))
Label: link
License: All rights reserved
LicenseURL: http://en.wikipedia.org/wiki/All_rights_reserved
objects: Sketcher::SketchObject×5, PartDesign::Pad×2, PartDesign::Groove×2, PartDesign::Mirrored×2, PartDesign::Body×2, PartDesign::Pocket×1, PartDesign::Fillet×1, App::Part×1
note: 21 computed .brp shape members not serialized (recipe doc carries the construction recipe); baked Part::Feature solids carry a one-line shape summary decoded from their .brp

FEATURE [Sketcher::SketchObject] Sketch
  FullyConstrained = true
  MapMode = 5
  Support = -> [XY_Plane001]
  sketch-geometry (4):
    g0: ArcOfCircle CenterX=-70 CenterY=0 CenterZ=0 NormalX=0 NormalY=0 NormalZ=1 AngleXU=0 Radius=8 StartAngle=0.384397 EndAngle=5.89879
    g1: ArcOfCircle CenterX=70 CenterY=0 CenterZ=0 NormalX=0 NormalY=0 NormalZ=1 AngleXU=0 Radius=8 StartAngle=3.52599 EndAngle=9.04038
    g2: LineSegment StartX=-62.5838 StartY=-3 StartZ=0 EndX=62.5838 EndY=-3 EndZ=0
    g3: LineSegment StartX=62.5838 StartY=3 StartZ=0 EndX=-62.5838 EndY=3 EndZ=0
  constraints (13):
    c: PointOnObject(g0,g-1)
    c: Symmetric(g0,g1,g-1)
    c: Equal(g0,g1)
    c: DistanceX(g0,g1) = 140
    c: Horizontal(g2)
    c: Horizontal(g3)
    c: Coincident(g0,g3)
    c: Coincident(g1,g2)
    c: Coincident(g2,g0)
    c: Vertical(g0,g0)
    c: Radius(g0) = 8
    c: Distance(g0,g0) = 6
    c: Coincident(g1,g3)
FEATURE [PartDesign::Pad] Pad
  Direction = (0,0,1)
  Length = 6
  Length2 = 4
  Midplane = true
  Profile = -> Sketch
  ReferenceAxis = -> Sketch [N_Axis]
  Refine = true
  Type = 4
FEATURE [Sketcher::SketchObject] Sketch001
  FullyConstrained = true
  MapMode = 5
  Placement = pos=(0,0,0) rot=(1,0,0;1.5708rad)
  Support = -> [XZ_Plane001]
  sketch-geometry (4):
    g0: ArcOfCircle CenterX=-70 CenterY=0 CenterZ=0 NormalX=0 NormalY=0 NormalZ=1 AngleXU=0 Radius=5 StartAngle=1.5708 EndAngle=3.54431
    g1: LineSegment StartX=-74.6 StartY=-1.95959 StartZ=0 EndX=-79.2421 EndY=-10 EndZ=0
    g2: LineSegment StartX=-79.2421 StartY=-10 StartZ=0 EndX=-70 EndY=-10 EndZ=0
    g3: LineSegment StartX=-70 StartY=5 StartZ=0 EndX=-70 EndY=-10 EndZ=0
  constraints (13):
    c: Coincident(g1,g2)
    c: Horizontal(g2)
    c: PointOnObject(g0,g-1)
    c: Coincident(g3,g0)
    c: Coincident(g3,g2)
    c: Vertical(g3)
    c: PointOnObject(g0,g3)
    c: Radius(g0) = 5
    c: DistanceX(g0,g2) = 4.6
    c: DistanceX(g0,g-1) = 70
    c: Angle(g1,g3) = 0.523599
    c: DistanceY(g3,g3) = 15
    c: Coincident(g1,g0)
FEATURE [PartDesign::Groove] Groove
  Angle = 360
  Angle2 = 60
  Axis = (0,-2e-16,-1)
  Base = (-70,1.1e-15,5)
  BaseFeature = -> Pad
  Profile = -> Sketch001
  ReferenceAxis = -> Sketch001 [Edge4]
  Refine = true
  Reversed = true
  Type = 0
FEATURE [Sketcher::SketchObject] Sketch003
  FullyConstrained = true
  MapMode = 5
  Support = -> [XY_Plane002]
  sketch-geometry (4):
    g0: ArcOfCircle CenterX=-70 CenterY=0 CenterZ=0 NormalX=0 NormalY=0 NormalZ=1 AngleXU=0 Radius=8 StartAngle=0.384397 EndAngle=5.89879
    g1: ArcOfCircle CenterX=70 CenterY=0 CenterZ=0 NormalX=0 NormalY=0 NormalZ=1 AngleXU=0 Radius=8 StartAngle=3.52599 EndAngle=9.04038
    g2: LineSegment StartX=-62.5838 StartY=-3 StartZ=0 EndX=62.5838 EndY=-3 EndZ=0
    g3: LineSegment StartX=62.5838 StartY=3 StartZ=0 EndX=-62.5838 EndY=3 EndZ=0
  constraints (13):
    c: PointOnObject(g0,g-1)
    c: Symmetric(g0,g1,g-1)
    c: Equal(g0,g1)
    c: DistanceX(g0,g1) = 140
    c: Horizontal(g2)
    c: Horizontal(g3)
    c: Coincident(g0,g3)
    c: Coincident(g1,g2)
    c: Coincident(g2,g0)
    c: Vertical(g0,g0)
    c: Radius(g0) = 8
    c: Distance(g0,g0) = 6
    c: Coincident(g1,g3)
FEATURE [PartDesign::Pad] Pad001
  Direction = (0,0,1)
  Length = 6
  Length2 = 4
  Midplane = true
  Profile = -> Sketch003
  ReferenceAxis = -> Sketch003 [N_Axis]
  Refine = true
  Type = 4
FEATURE [Sketcher::SketchObject] Sketch004
  FullyConstrained = true
  MapMode = 5
  Placement = pos=(0,0,0) rot=(1,0,0;1.5708rad)
  Support = -> [XZ_Plane001]
  sketch-geometry (4):
    g0: ArcOfCircle CenterX=-70 CenterY=0 CenterZ=0 NormalX=0 NormalY=0 NormalZ=1 AngleXU=0 Radius=5 StartAngle=1.5708 EndAngle=3.54431
    g1: LineSegment StartX=-74.6 StartY=-1.95959 StartZ=0 EndX=-79.2421 EndY=-10 EndZ=0
    g2: LineSegment StartX=-79.2421 StartY=-10 StartZ=0 EndX=-70 EndY=-10 EndZ=0
    g3: LineSegment StartX=-70 StartY=5 StartZ=0 EndX=-70 EndY=-10 EndZ=0
  constraints (13):
    c: Coincident(g1,g2)
    c: Horizontal(g2)
    c: PointOnObject(g0,g-1)
    c: Coincident(g3,g0)
    c: Coincident(g3,g2)
    c: Vertical(g3)
    c: PointOnObject(g0,g3)
    c: Radius(g0) = 5
    c: DistanceX(g0,g2) = 4.6
    c: DistanceX(g0,g-1) = 70
    c: Angle(g1,g3) = 0.523599
    c: DistanceY(g3,g3) = 15
    c: Coincident(g1,g0)
FEATURE [PartDesign::Groove] Groove001
  Angle = 360
  Angle2 = 60
  Axis = (0,-2e-16,-1)
  Base = (-70,1.1e-15,5)
  BaseFeature = -> Pad001
  Profile = -> Sketch004
  ReferenceAxis = -> Sketch004 [Edge4]
  Refine = true
  Reversed = true
  Type = 0
FEATURE [Sketcher::SketchObject] Sketch005
  ExternalGeometry = -> [Sketch004]
  FullyConstrained = true
  MapMode = 5
  Placement = pos=(0,0,-4) rot=(1,0,0;3.14159rad)
  Support = -> [Groove001]
  sketch-geometry (4):
    g0: LineSegment StartX=-71 StartY=0.5 StartZ=0 EndX=-81 EndY=0.5 EndZ=0
    g1: LineSegment StartX=-81 StartY=0.5 StartZ=0 EndX=-81 EndY=-0.5 EndZ=0
    g2: LineSegment StartX=-81 StartY=-0.5 StartZ=0 EndX=-71 EndY=-0.5 EndZ=0
    g3: LineSegment StartX=-71 StartY=-0.5 StartZ=0 EndX=-71 EndY=0.5 EndZ=0
  constraints (11):
    c: Coincident(g0,g1)
    c: Coincident(g1,g2)
    c: Coincident(g2,g3)
    c: Coincident(g3,g0)
    c: Horizontal(g0)
    c: Horizontal(g2)
    c: Vertical(g1)
    c: Symmetric(g2,g0,g-1)
    c: Distance(g3,g3) = 1
    c: DistanceX(g2,g-3) = 1
    c: DistanceX(g2,g2) = 10
FEATURE [PartDesign::Pocket] Pocket
  BaseFeature = -> Groove001
  Direction = (0,0,1)
  Length = 8
  Length2 = 5
  Profile = -> Sketch005
  ReferenceAxis = -> Sketch005 [N_Axis]
  Refine = true
  Type = 0
FEATURE [PartDesign::Mirrored] Mirrored
  BaseFeature = -> Groove
  MirrorPlane = -> Sketch001 [V_Axis]
  Originals = -> [Groove]
  Refine = true
FEATURE [PartDesign::Body] Body  label="link-skel"
  Group = -> [Sketch,Pad,Sketch001,Groove,Mirrored]
  Origin = -> Origin001
  Tip = -> Mirrored
FEATURE [PartDesign::Mirrored] Mirrored001
  BaseFeature = -> Pocket
  MirrorPlane = -> Sketch005 [V_Axis]
  Originals = -> [Pocket,Groove001]
  Refine = true
FEATURE [PartDesign::Fillet] Fillet
  Base = -> Mirrored001 [Edge6,Edge8,Edge31,Edge27]
  BaseFeature = -> Mirrored001
  Radius = 10
  Refine = true
  SupportTransform = false
  UseAllEdges = false
FEATURE [PartDesign::Body] Body001  label="link0"
  Group = -> [Sketch003,Pad001,Sketch004,Groove001,Sketch005,Pocket,Mirrored001,Fillet]
  Origin = -> Origin002
  Tip = -> Fillet
FEATURE [App::Part] Part  label="link"
  Group = -> [Body,Body001]
  Origin = -> Origin
---- part nema17-48.FCStd = doc fcstd_b35fc45cbd58 ----
FCSTD DOCUMENT  (FreeCAD 0.22R35451 (Git))
Label: nema17-48
License: All rights reserved
LicenseURL: http://en.wikipedia.org/wiki/All_rights_reserved
objects: Sketcher::SketchObject×4, PartDesign::Pad×3, PartDesign::Chamfer×2, PartDesign::Hole×1, PartDesign::Body×1, App::Part×1
note: 17 computed .brp shape members not serialized (recipe doc carries the construction recipe); baked Part::Feature solids carry a one-line shape summary decoded from their .brp

FEATURE [Sketcher::SketchObject] Sketch
  FullyConstrained = false
  MapMode = 5
  Support = -> [XY_Plane]
  sketch-geometry (5):
    g0: LineSegment StartX=21.15 StartY=21.15 StartZ=0 EndX=-21.15 EndY=21.15 EndZ=0
    g1: LineSegment StartX=-21.15 StartY=21.15 StartZ=0 EndX=-21.15 EndY=-21.15 EndZ=0
    g2: LineSegment StartX=-21.15 StartY=-21.15 StartZ=0 EndX=21.15 EndY=-21.15 EndZ=0
    g3: LineSegment StartX=21.15 StartY=-21.15 StartZ=0 EndX=21.15 EndY=21.15 EndZ=0
    g4: Circle CenterX=0 CenterY=0 CenterZ=0 NormalX=0 NormalY=0 NormalZ=1 AngleXU=0 Radius=29.9106
  constraints (14):
    c: Coincident(g0,g1)
    c: Coincident(g1,g2)
    c: Coincident(g2,g3)
    c: Coincident(g3,g0)
    c: Equal(g0,g1)
    c: Equal(g0,g2)
    c: Equal(g0,g3)
    c: PointOnObject(g0,g4)
    c: PointOnObject(g1,g4)
    c: PointOnObject(g2,g4)
    c: PointOnObject(g3,g4)
    c: Coincident(g4,g-1)
    c: Horizontal(g0)
    c: DistanceY(g3,g3) = 42.3
FEATURE [PartDesign::Pad] Pad
  Direction = (0,0,1)
  Length = 48
  Length2 = 100
  Profile = -> Sketch
  ReferenceAxis = -> Sketch [N_Axis]
  Type = 0
FEATURE [Sketcher::SketchObject] Sketch001
  FullyConstrained = true
  MapMode = 5
  Placement = pos=(0,0,48) rot=(0,0,1;0rad)
  Support = -> [Pad]
  sketch-geometry (1):
    g0: Circle CenterX=0 CenterY=0 CenterZ=0 NormalX=0 NormalY=0 NormalZ=1 AngleXU=0 Radius=11
  constraints (2):
    c: Coincident(g0,g-1)
    c: Diameter(g0) = 22
FEATURE [PartDesign::Pad] Pad001
  BaseFeature = -> Pad
  Direction = (0,0,1)
  Length = 2
  Length2 = 100
  Profile = -> Sketch001
  ReferenceAxis = -> Sketch001 [N_Axis]
  Type = 0
FEATURE [Sketcher::SketchObject] Sketch002
  FullyConstrained = true
  MapMode = 5
  Placement = pos=(0,0,48) rot=(0,0,1;0rad)
  Support = -> [Pad001]
  sketch-geometry (1):
    g0: Circle CenterX=0 CenterY=0 CenterZ=0 NormalX=0 NormalY=0 NormalZ=1 AngleXU=0 Radius=2.5
  constraints (2):
    c: Coincident(g0,g-1)
    c: Diameter(g0) = 5
FEATURE [PartDesign::Pad] Pad002
  BaseFeature = -> Pad001
  Direction = (0,0,1)
  Length = 24
  Length2 = 100
  Profile = -> Sketch002
  ReferenceAxis = -> Sketch002 [N_Axis]
  Type = 0
FEATURE [PartDesign::Chamfer] Chamfer
  Angle = 45
  Base = -> Pad002 [Edge18]
  BaseFeature = -> Pad002
  ChamferType = 0
  FlipDirection = false
  Size = 0.5
  Size2 = 1
  SupportTransform = true
  UseAllEdges = false
FEATURE [Sketcher::SketchObject] Sketch004
  FullyConstrained = true
  MapMode = 5
  Placement = pos=(0,0,48) rot=(0,0,1;0rad)
  sketch-geometry (4):
    g0: Circle CenterX=15.5 CenterY=-15.5 CenterZ=0 NormalX=0 NormalY=0 NormalZ=1 AngleXU=0 Radius=1.25
    g1: Circle CenterX=15.5 CenterY=15.5 CenterZ=0 NormalX=0 NormalY=0 NormalZ=1 AngleXU=0 Radius=1.25
    g2: Circle CenterX=-15.5 CenterY=15.5 CenterZ=0 NormalX=0 NormalY=0 NormalZ=1 AngleXU=0 Radius=1.25
    g3: Circle CenterX=-15.5 CenterY=-15.5 CenterZ=0 NormalX=0 NormalY=0 NormalZ=1 AngleXU=0 Radius=1.25
  constraints (9):
    c: Diameter(g0) = 2.5
    c: Symmetric(g1,g0,g-1)
    c: Symmetric(g1,g2,g-2)
    c: Symmetric(g3,g2,g-1)
    c: Equal(g2,g1)
    c: Equal(g1,g3)
    c: Equal(g3,g0)
    c: DistanceX(g2,g1) = 31
    c: DistanceY(g0,g1) = 31
FEATURE [PartDesign::Hole] Hole
  BaseFeature = -> Chamfer
  CustomThreadClearance = 0
  Depth = 4
  DepthType = 0
  Diameter = 3.4
  DrillForDepth = false
  DrillPoint = 1
  DrillPointAngle = 118
  HoleCutCountersinkAngle = 90
  HoleCutCustomValues = false
  HoleCutDepth = 0
  HoleCutDiameter = 1.6
  HoleCutType = 0
  ModelThread = false
  Profile = -> Sketch004
  Tapered = false
  TaperedAngle = 90
  ThreadClass = 0
  ThreadDepth = 4
  ThreadDepthType = 0
  ThreadDirection = 0
  ThreadFit = 0
  ThreadSize = 9
  ThreadType = 1
  Threaded = false
  UseCustomThreadClearance = false
FEATURE [PartDesign::Chamfer] Chamfer001
  Angle = 45
  Base = -> Hole [Edge20,Edge17,Edge22,Edge18]
  BaseFeature = -> Hole
  ChamferType = 0
  FlipDirection = false
  Size = 5
  Size2 = 1
  SupportTransform = true
  UseAllEdges = false
FEATURE [PartDesign::Body] Body  label="nema17"
  Group = -> [Sketch,Pad,Sketch001,Pad001,Sketch002,Pad002,Chamfer,Sketch004,Hole,Chamfer001]
  Origin = -> Origin
  Placement = pos=(0,0,-50) rot=(0,0,1;0rad)
  Tip = -> Chamfer001
FEATURE [App::Part] Part  label="nema17-48"
  Group = -> [Body]
  Origin = -> Origin001
---- part plate.FCStd = doc fcstd_dd23bfd2ac05 ----
FCSTD DOCUMENT  (FreeCAD 2024.1R35694 (Git))
Label: plate
License: All rights reserved
LicenseURL: http://en.wikipedia.org/wiki/All_rights_reserved
objects: Sketcher::SketchObject×6, PartDesign::PolarPattern×3, PartDesign::Pad×2, PartDesign::Revolution×2, PartDesign::Body×2, PartDesign::Chamfer×2, PartDesign::Pocket×2, App::Part×1
note: 27 computed .brp shape members not serialized (recipe doc carries the construction recipe); baked Part::Feature solids carry a one-line shape summary decoded from their .brp

FEATURE [Sketcher::SketchObject] Sketch003
  FullyConstrained = true
  MapMode = 5
  Support = -> [XY_Plane002]
  sketch-geometry (4):
    g0: LineSegment StartX=19 StartY=0 StartZ=0 EndX=19 EndY=50 EndZ=0
    g1: LineSegment StartX=19 StartY=50 StartZ=0 EndX=-19 EndY=50 EndZ=0
    g2: LineSegment StartX=-19 StartY=50 StartZ=0 EndX=-19 EndY=0 EndZ=0
    g3: LineSegment StartX=-19 StartY=0 StartZ=0 EndX=19 EndY=0 EndZ=0
  constraints (11):
    c: Coincident(g0,g1)
    c: Coincident(g1,g2)
    c: Coincident(g2,g3)
    c: Coincident(g3,g0)
    c: Vertical(g0)
    c: Vertical(g2)
    c: Horizontal(g1)
    c: PointOnObject(g0,g-1)
    c: Symmetric(g2,g0,g-2)
    c: DistanceX(g3,g3) = 38
    c: DistanceY(g0,g0) = 50
FEATURE [PartDesign::Pad] Pad001
  Direction = (0,0,1)
  Length = 6
  Length2 = 10
  Profile = -> Sketch003
  ReferenceAxis = -> Sketch003 [N_Axis]
  Type = 0
FEATURE [Sketcher::SketchObject] Sketch
  ExternalGeometry = -> [Pad001]
  FullyConstrained = true
  MapMode = 5
  Support = -> [XY_Plane002]
  sketch-geometry (4):
    g0: LineSegment StartX=-30 StartY=50 StartZ=0 EndX=30 EndY=50 EndZ=0
    g1: ArcOfCircle CenterX=-25 CenterY=50 CenterZ=0 NormalX=0 NormalY=0 NormalZ=1 AngleXU=0 Radius=5 StartAngle=0.643501 EndAngle=3.14159
    g2: ArcOfCircle CenterX=25 CenterY=50 CenterZ=0 NormalX=0 NormalY=0 NormalZ=1 AngleXU=0 Radius=5 StartAngle=-9e-16 EndAngle=2.49809
    g3: LineSegment StartX=-21 StartY=53 StartZ=0 EndX=21 EndY=53 EndZ=0
  constraints (12):
    c: Symmetric(g0,g0,g-2)
    c: PointOnObject(g-3,g0)
    c: PointOnObject(g1,g0)
    c: Coincident(g1,g0)
    c: Coincident(g2,g0)
    c: Symmetric(g1,g2,g-2)
    c: DistanceX(g1,g2) = 50
    c: Radius(g1) = 5
    c: Coincident(g3,g1)
    c: Coincident(g3,g2)
    c: Horizontal(g3)
    c: DistanceY(g-3,g1) = 3
FEATURE [PartDesign::Revolution] Revolution
  Angle = 360
  Angle2 = 60
  Axis = (1,-1e-16,0)
  Base = (-30,50,0)
  BaseFeature = -> Pad001
  Profile = -> Sketch
  ReferenceAxis = -> Sketch [Edge1]
  Refine = true
  Type = 0
FEATURE [PartDesign::PolarPattern] PolarPattern
  Angle = 360
  Axis = -> Sketch003 [N_Axis]
  BaseFeature = -> Revolution
  Mode = 0
  Occurrences = 3
  Offset = 120
  Originals = -> [Pad001,Revolution]
  Refine = true
FEATURE [PartDesign::Body] Body001  label="plate-skel"
  Group = -> [Sketch003,Pad001,Sketch,Revolution,PolarPattern]
  Origin = -> Origin002
  Tip = -> PolarPattern
FEATURE [Sketcher::SketchObject] Sketch005
  FullyConstrained = true
  MapMode = 5
  Support = -> [XY_Plane003]
  sketch-geometry (4):
    g0: LineSegment StartX=15 StartY=0 StartZ=0 EndX=15 EndY=50 EndZ=0
    g1: LineSegment StartX=15 StartY=50 StartZ=0 EndX=-15 EndY=50 EndZ=0
    g2: LineSegment StartX=-15 StartY=50 StartZ=0 EndX=-15 EndY=0 EndZ=0
    g3: LineSegment StartX=-15 StartY=0 StartZ=0 EndX=15 EndY=0 EndZ=0
  constraints (11):
    c: Coincident(g0,g1)
    c: Coincident(g1,g2)
    c: Coincident(g2,g3)
    c: Coincident(g3,g0)
    c: Vertical(g0)
    c: Vertical(g2)
    c: Horizontal(g1)
    c: PointOnObject(g0,g-1)
    c: Symmetric(g2,g0,g-2)
    c: DistanceX(g3,g3) = 30
    c: DistanceY(g0,g0) = 50
FEATURE [PartDesign::Pad] Pad002
  Direction = (0,0,1)
  Length = 6
  Length2 = 10
  Profile = -> Sketch005
  ReferenceAxis = -> Sketch005 [N_Axis]
  Type = 0
FEATURE [Sketcher::SketchObject] Sketch004
  ExternalGeometry = -> [Pad002]
  FullyConstrained = true
  MapMode = 5
  Support = -> [XY_Plane003]
  sketch-geometry (4):
    g0: LineSegment StartX=-29.9 StartY=50 StartZ=0 EndX=29.9 EndY=50 EndZ=0
    g1: ArcOfCircle CenterX=-25 CenterY=50 CenterZ=0 NormalX=0 NormalY=0 NormalZ=1 AngleXU=0 Radius=4.9 StartAngle=0.658897 EndAngle=3.14159
    g2: ArcOfCircle CenterX=25 CenterY=50 CenterZ=0 NormalX=0 NormalY=0 NormalZ=1 AngleXU=0 Radius=4.9 StartAngle=4e-16 EndAngle=2.4827
    g3: LineSegment StartX=-21.1257 StartY=53 StartZ=0 EndX=21.1257 EndY=53 EndZ=0
  constraints (12):
    c: Symmetric(g0,g0,g-2)
    c: PointOnObject(g-3,g0)
    c: PointOnObject(g1,g0)
    c: Coincident(g1,g0)
    c: Coincident(g2,g0)
    c: Symmetric(g1,g2,g-2)
    c: DistanceX(g1,g2) = 50
    c: Radius(g1) = 4.9
    c: Coincident(g3,g1)
    c: Coincident(g3,g2)
    c: Horizontal(g3)
    c: DistanceY(g-3,g1) = 3
FEATURE [PartDesign::Revolution] Revolution001
  Angle = 360
  Angle2 = 60
  Axis = (1,0,0)
  Base = (-29.9,50,0)
  BaseFeature = -> Pad002
  Profile = -> Sketch004
  ReferenceAxis = -> Sketch004 [Edge1]
  Refine = true
  Type = 0
FEATURE [PartDesign::PolarPattern] PolarPattern001
  Angle = 360
  Axis = -> Sketch005 [N_Axis]
  BaseFeature = -> Revolution001
  Mode = 0
  Occurrences = 3
  Offset = 120
  Originals = -> [Pad002,Revolution001]
  Refine = true
FEATURE [PartDesign::Chamfer] Chamfer
  Angle = 45
  Base = -> PolarPattern001 [Edge17,Edge44,Edge35]
  BaseFeature = -> PolarPattern001
  ChamferType = 0
  FlipDirection = false
  Refine = true
  Size = 2.4
  Size2 = 1
  SupportTransform = false
  UseAllEdges = false
FEATURE [Sketcher::SketchObject] Sketch006
  FullyConstrained = true
  MapMode = 5
  Placement = pos=(0,0,0) rot=(1,0,0;3.14159rad)
  Support = -> [Chamfer]
  sketch-geometry (7):
    g0: LineSegment StartX=25.9808 StartY=45 StartZ=0 EndX=-25.9808 EndY=45 EndZ=0
    g1: LineSegment StartX=-25.9808 StartY=45 StartZ=0 EndX=-51.9615 EndY=0 EndZ=0
    g2: LineSegment StartX=-51.9615 StartY=0 StartZ=0 EndX=-25.9808 EndY=-45 EndZ=0
    g3: LineSegment StartX=-25.9808 StartY=-45 StartZ=0 EndX=25.9808 EndY=-45 EndZ=0
    g4: LineSegment StartX=25.9808 StartY=-45 StartZ=0 EndX=51.9615 EndY=0 EndZ=0
    g5: LineSegment StartX=51.9615 StartY=0 StartZ=0 EndX=25.9808 EndY=45 EndZ=0
    g6: Circle CenterX=0 CenterY=0 CenterZ=0 NormalX=0 NormalY=0 NormalZ=1 AngleXU=0 Radius=51.9615
  constraints (16):
    c: Coincident(g0,g1)
    c: Coincident(g1,g2)
    c: Coincident(g2,g3)
    c: Coincident(g3,g4)
    c: Coincident(g4,g5)
    c: Coincident(g5,g0)
    c: Equal(g0, g1-g5) x5
    c: PointOnObject(g0,g6)
    c: PointOnObject(g1,g6)
    c: PointOnObject(g2,g6)
    c: PointOnObject(g3,g6)
    c: PointOnObject(g4,g6)
    c: PointOnObject(g5,g6)
    c: Coincident(g6,g-1)
    c: Horizontal(g0)
    c: DistanceY(g3,g0) = 90
FEATURE [PartDesign::Pocket] Pocket
  BaseFeature = -> Chamfer
  Direction = (0,0,1)
  Length = 3
  Length2 = 5
  Profile = -> Sketch006
  ReferenceAxis = -> Sketch006 [N_Axis]
  Refine = true
  Type = 0
FEATURE [Sketcher::SketchObject] Sketch007
  FullyConstrained = true
  MapMode = 5
  Placement = pos=(0,0,3) rot=(1,0,0;3.14159rad)
  Support = -> [Pocket]
  sketch-geometry (6):
    g0: Circle CenterX=-6.25 CenterY=-37.5 CenterZ=0 NormalX=0 NormalY=0 NormalZ=1 AngleXU=0 Radius=3.5
    g1: Circle CenterX=6.25 CenterY=-37.5 CenterZ=0 NormalX=0 NormalY=0 NormalZ=1 AngleXU=0 Radius=3.5
    g2: Circle CenterX=-6.25 CenterY=-25 CenterZ=0 NormalX=0 NormalY=0 NormalZ=1 AngleXU=0 Radius=3.5
    g3: Circle CenterX=6.25 CenterY=-25 CenterZ=0 NormalX=0 NormalY=0 NormalZ=1 AngleXU=0 Radius=3.5
    g4: Circle CenterX=6.25 CenterY=-12.5 CenterZ=0 NormalX=0 NormalY=0 NormalZ=1 AngleXU=0 Radius=3.5
    g5: Circle CenterX=-6.25 CenterY=-12.5 CenterZ=0 NormalX=0 NormalY=0 NormalZ=1 AngleXU=0 Radius=3.5
  constraints (15):
    c: Symmetric(g0,g1,g-2)
    c: Symmetric(g2,g3,g-2)
    c: DistanceX(g2,g3) = 12.5
    c: DistanceY(g1,g3) = 12.5
    c: Diameter(g3) = 7
    c: Equal(g2,g3)
    c: Equal(g0,g1)
    c: DistanceY(g3,g-1) = 25
    c: Vertical(g3,g1)
    c: Equal(g0,g2)
    c: Symmetric(g5,g4,g-2)
    c: Vertical(g2,g5)
    c: DistanceY(g3,g4) = 12.5
    c: Equal(g5,g2)
    c: Equal(g4,g5)
FEATURE [PartDesign::Pocket] Pocket001
  BaseFeature = -> Pocket
  Direction = (0,0,1)
  Length = 5
  Length2 = 5
  Profile = -> Sketch007
  ReferenceAxis = -> Sketch007 [N_Axis]
  Refine = true
  Type = 1
FEATURE [PartDesign::PolarPattern] PolarPattern002
  Angle = 360
  Axis = -> Z_Axis003
  BaseFeature = -> Pocket001
  Mode = 0
  Occurrences = 3
  Offset = 120
  Originals = -> [Pocket001]
  Refine = true
FEATURE [PartDesign::Chamfer] Chamfer001
  Angle = 45
  Base = -> PolarPattern002 [Edge68,Edge120,Edge121]
  BaseFeature = -> PolarPattern002
  ChamferType = 0
  FlipDirection = false
  Refine = true
  Size = 1
  Size2 = 1
  SupportTransform = false
  UseAllEdges = false
FEATURE [PartDesign::Body] Body002  label="plate-0"
  Group = -> [Sketch005,Pad002,Sketch004,Revolution001,PolarPattern001,Chamfer,Sketch006,Pocket,Sketch007,Pocket001,PolarPattern002,Chamfer001]
  Origin = -> Origin003
  Tip = -> Chamfer001
FEATURE [App::Part] Part  label="plate"
  Group = -> [Body001,Body002]
  Origin = -> Origin001
